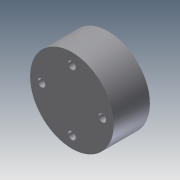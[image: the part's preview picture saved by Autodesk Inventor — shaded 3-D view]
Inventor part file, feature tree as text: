
AUTODESK INVENTOR PART (.ipt)
format: ipt  version: 2011 (Build 150239000, 239)  size: 102,912 bytes
history: native  units: in
note: dims shown in document units (in); Inventor stores cm internally (conversion verified against a paired STEP export)
features: extrude x4, sketch x4
ambient origin geometry x8: Origin, YZ Plane, XZ Plane, XY Plane, X Axis, Y Axis, Z Axis, Center Point
bodies: Solid1 (feature_tree)
feature tree (8):
  extrude  "Extrusion1"  Depth=0.3937in TaperAngle=0.0deg
  extrude  "Extrusion2"  Depth=0.0787in
  extrude  "Extrusion3"  Depth=0.0787in
  extrude  "Extrusion4"  Depth=0.3937in TaperAngle=0.0deg
  sketch  "Sketch1"  dims[d0=0.8661in d1=0.3937in d2=0.0in]
  sketch  "Sketch2"  dims[d3=0.6299in d4=0.0787in]
  sketch  "Sketch3"  dims[d5=0.0787in d6=0.0787in]
  sketch  "Sketch4"  dims[d7=0.0787in d8=0.3937in d9=0.0in d10=0.375in d11=0.0in d12=0.375in d13=0.0in]
